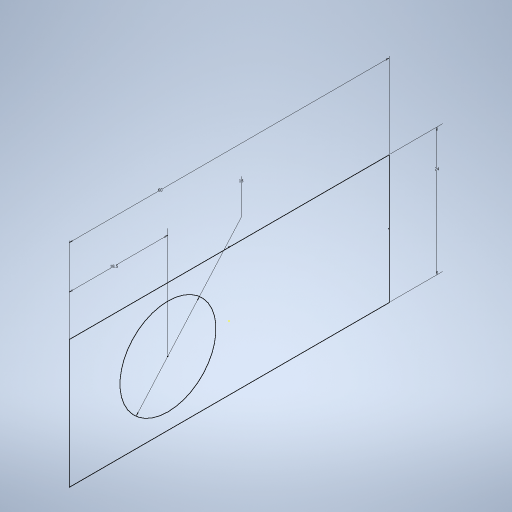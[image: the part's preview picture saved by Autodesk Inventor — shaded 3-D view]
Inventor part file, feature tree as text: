
AUTODESK INVENTOR PART (.ipt)
format: ipt  version: 2024.1 (Build 281209000, 209)  size: 237,568 bytes
history: native  units: mm
features: sketch x1
ambient origin geometry x8: Origin, YZ Plane, XZ Plane, XY Plane, X Axis, Y Axis, Z Axis, Center Point
feature tree (1):
  sketch  "Boceto1"  dims[d0=60.0mm d1=24.0mm d2=18.0mm d3=18.5mm]
